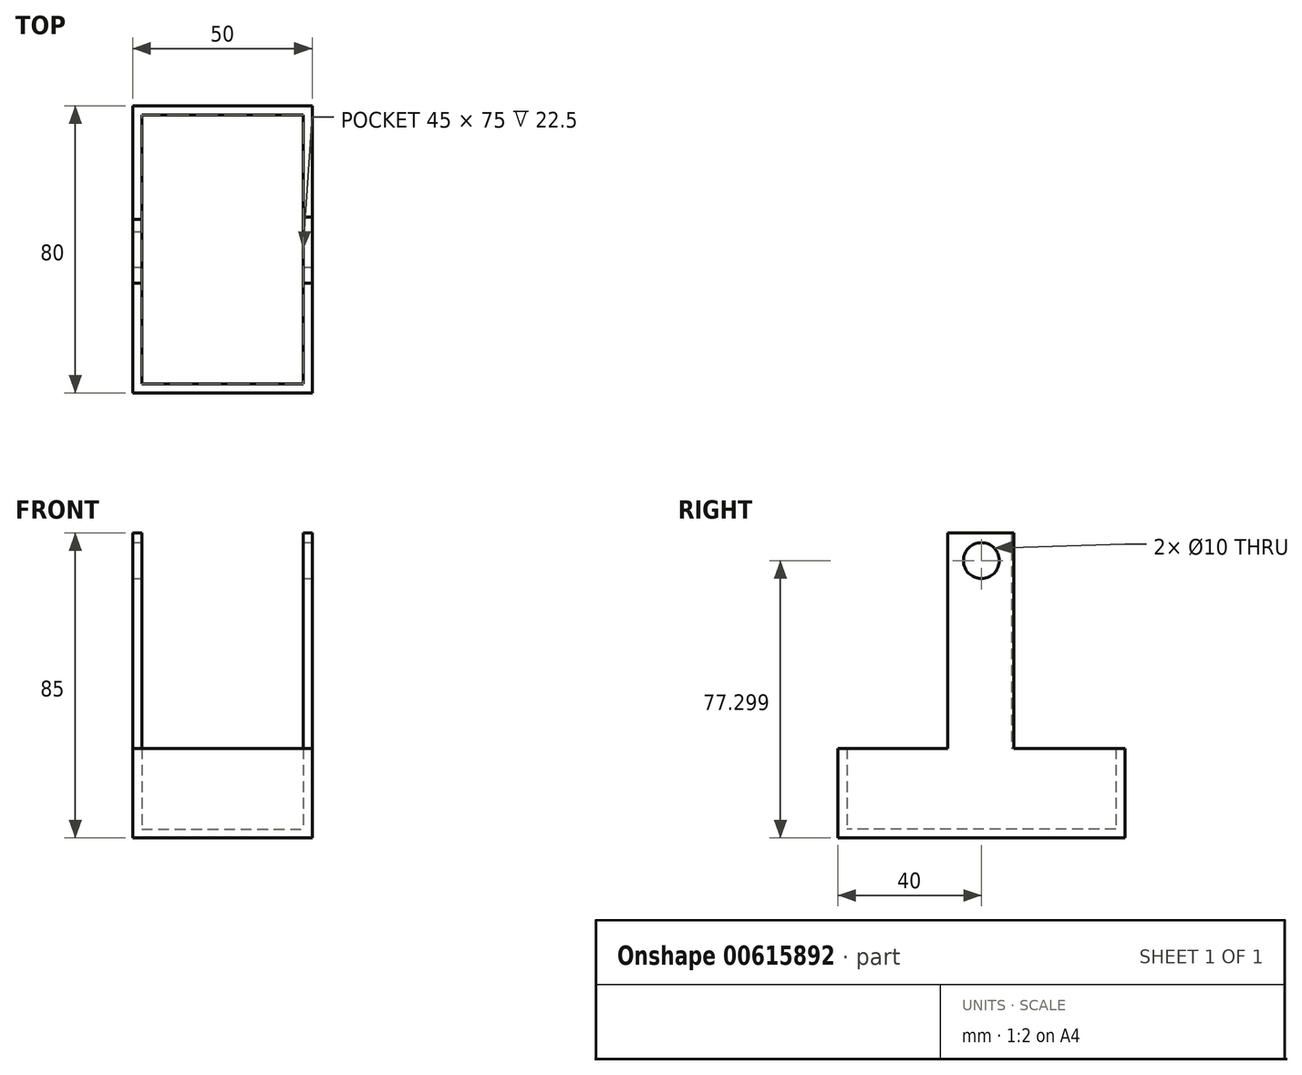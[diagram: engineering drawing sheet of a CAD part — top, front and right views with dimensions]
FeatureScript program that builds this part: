
annotation { "Feature Type Name" : "Feature", "Feature Type Description" : "" }
export const myFeature = defineFeature(function(context is Context, id is Id, definition is map)
    precondition{}
    {
        {
            var Q0;
            Q0=qCreatedBy(makeId("Top.planeOp"),FACE);
            var sketch = newSketch(context, id + "F0", { "sketchPlane" : qUnion([Q0])});
            skLineSegment(sketch, "E0.bottom", {"start": v(-25, 40) * mm, "end": v(25, 40) * mm});
            skLineSegment(sketch, "E0.top", {"start": v(-25, -40) * mm, "end": v(25, -40) * mm});
            skLineSegment(sketch, "E0.left", {"start": v(-25, 40) * mm, "end": v(-25, -40) * mm});
            skLineSegment(sketch, "E0.right", {"start": v(25, 40) * mm, "end": v(25, -40) * mm});
            skPoint(sketch, "E0.middle", {"position": v(0, 0) * mm});
            skSolve(sketch);
        }
        {
            var Q0;
            Q0=makeQuery(id+"F0.imprint","IMPRINT",FACE,{"disambiguationData":[TD([[makeQuery(id+"F0.imprint","IMPRINT",EDGE,{"derivedFrom":sQuery(id+"F0.wireOp",EDGE,"E0.bottom")}),-1.0]])]});
            extrude(context, id + "F1", {"entities" : qUnion([Q0]), "depth" : 25 * mm, "offsetDistance" : 25 * mm});
        }
        {
            var Q0;
            Q0=makeQuery(id+"F1.opExtrude","CAP_FACE",FACE,{"disambiguationData":[OSD([sQuery(id+"F0.wireOp",EDGE,"E0.bottom"),sQuery(id+"F0.wireOp",EDGE,"E0.top"),sQuery(id+"F0.wireOp",EDGE,"E0.left"),sQuery(id+"F0.wireOp",EDGE,"E0.right")])],"isStart":false});
            shell(context, id + "F2", {"entities" : qUnion([Q0]), "thickness" : 2.5 * mm});
        }
        {
            var Q0;
            Q0=makeQuery(id+"F1.opExtrude","CAP_FACE",FACE,{"disambiguationData":[OSD([sQuery(id+"F0.wireOp",EDGE,"E0.bottom"),sQuery(id+"F0.wireOp",EDGE,"E0.top"),sQuery(id+"F0.wireOp",EDGE,"E0.left"),sQuery(id+"F0.wireOp",EDGE,"E0.right")])],"isStart":false});
            var sketch = newSketch(context, id + "F3", { "sketchPlane" : qUnion([Q0])});
            skLineSegment(sketch, "E1.bottom", {"start": v(-22.5, -9.44) * mm, "end": v(-25, -9.44) * mm});
            skLineSegment(sketch, "E1.top", {"start": v(-22.5, 8.4) * mm, "end": v(-25, 8.4) * mm});
            skLineSegment(sketch, "E1.left", {"start": v(-22.5, -9.44) * mm, "end": v(-22.5, 8.4) * mm});
            skLineSegment(sketch, "E1.right", {"start": v(-25, -9.44) * mm, "end": v(-25, 8.4) * mm});
            skLineSegment(sketch, "E2.bottom", {"start": v(22.5, -9.44) * mm, "end": v(25, -9.44) * mm});
            skLineSegment(sketch, "E2.top", {"start": v(22.5, 9) * mm, "end": v(25, 9) * mm});
            skLineSegment(sketch, "E2.left", {"start": v(22.5, -9.44) * mm, "end": v(22.5, 9) * mm});
            skLineSegment(sketch, "E2.right", {"start": v(25, -9.44) * mm, "end": v(25, 9) * mm});
            skSolve(sketch);
        }
        {
            var Q0;
            Q0=makeQuery(id+"F3.imprint","IMPRINT",FACE,{"disambiguationData":[TD([[makeQuery(id+"F3.imprint","IMPRINT",EDGE,{"derivedFrom":sQuery(id+"F3.wireOp",EDGE,"E1.bottom")}),-1.0]])]});
            var Q1;
            Q1=makeQuery(id+"F3.imprint","IMPRINT",FACE,{"disambiguationData":[TD([[makeQuery(id+"F3.imprint","IMPRINT",EDGE,{"derivedFrom":sQuery(id+"F3.wireOp",EDGE,"E2.bottom")}),1.0]])]});
            extrude(context, id + "F4", {"entities" : qUnion([Q0, Q1]), "operationType" : NewBodyOperationType.ADD, "depth" : 60 * mm, "offsetDistance" : 25 * mm});
        }
        {
            var Q0;
            Q0=makeQuery(id+"F4.boolean.opBoolean","MERGE",FACE,{"derivedFrom":[makeQuery(id+"F1.opExtrude","SWEPT_FACE",FACE,{"disambiguationData":[OSD([sQuery(id+"F0.wireOp",EDGE,"E0.right")])]}),makeQuery(id+"F4.opExtrude","SWEPT_FACE",FACE,{"disambiguationData":[OSD([sQuery(id+"F3.wireOp",EDGE,"E2.right")])]})]});
            var sketch = newSketch(context, id + "F5", { "sketchPlane" : qUnion([Q0])});
            skPoint(sketch, "E3", {"position": v(0, 77.3) * mm});
            skSolve(sketch);
        }
        {
            var Q0;
            Q0=sQuery(id+"F5.wireOp",VERTEX,"E3");
            var Q1;
            Q1=makeQuery(id+"F1.opExtrude","SWEPT_BODY",BODY,{"disambiguationData":[OSD([sQuery(id+"F0.wireOp",EDGE,"E0.bottom"),sQuery(id+"F0.wireOp",EDGE,"E0.top"),sQuery(id+"F0.wireOp",EDGE,"E0.left"),sQuery(id+"F0.wireOp",EDGE,"E0.right")])]});
            hole(context, id + "F6", {"style" : HoleStyle.SIMPLE, "endStyle" : HoleEndStyle.THROUGH, "holeDiameter" : 10 * mm, "majorDiameter" : 5 * mm, "isTappedThrough" : true, "tappedDepth" : 12 * mm, "tapClearance" : 3, "locations" : qUnion([Q0]), "scope" : qUnion([Q1])});
        }
    });
